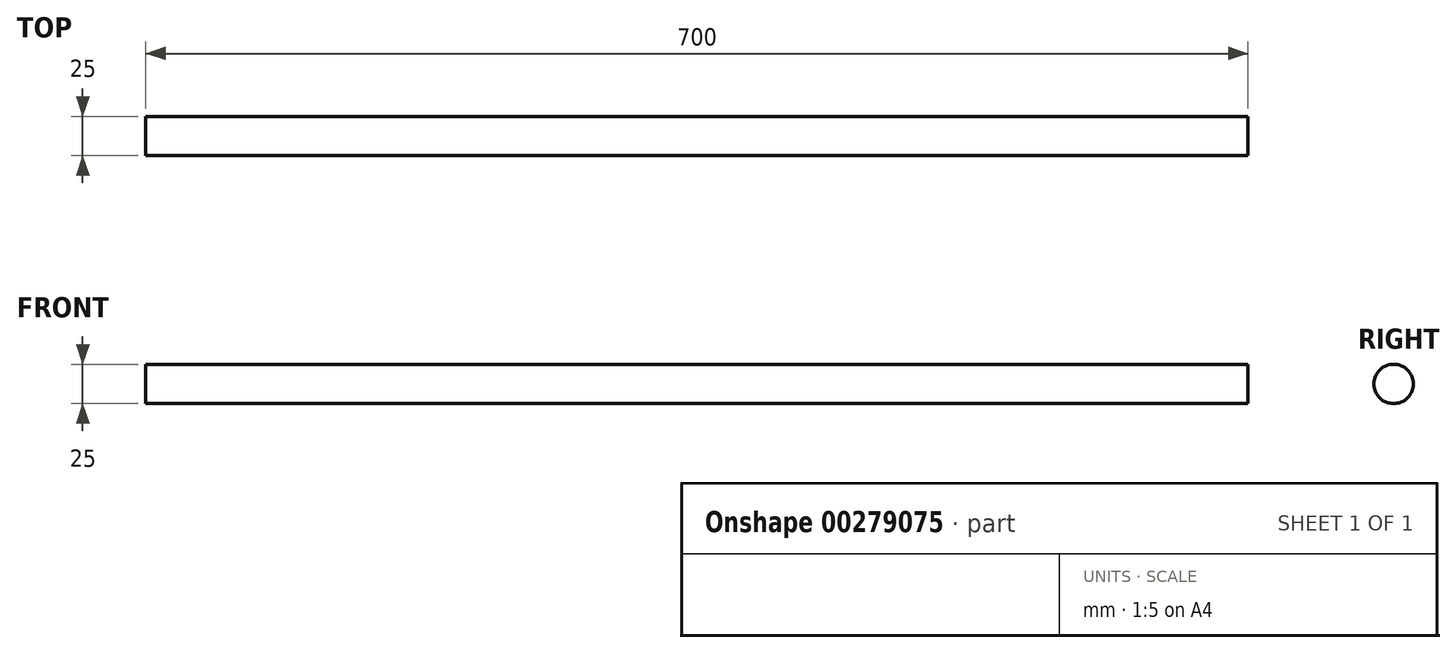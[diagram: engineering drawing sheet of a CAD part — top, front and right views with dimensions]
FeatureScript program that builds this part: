
annotation { "Feature Type Name" : "Feature", "Feature Type Description" : "" }
export const myFeature = defineFeature(function(context is Context, id is Id, definition is map)
    precondition{}
    {
        {
            var Q0;
            Q0=qCreatedBy(makeId("Right.planeOp"),FACE);
            var sketch = newSketch(context, id + "F0", { "sketchPlane" : qUnion([Q0])});
            skCircle(sketch, "E0", {"center": v(0, 0) * mm, "radius": 12.5 * mm});
            skSolve(sketch);
        }
        {
            var Q0;
            Q0=makeQuery(id+"F0.imprint","IMPRINT",FACE,{"disambiguationData":[TD([[makeQuery(id+"F0.imprint","IMPRINT",EDGE,{"derivedFrom":sQuery(id+"F0.wireOp",EDGE,"E0")}),1.0]])]});
            var Q1;
            Q1=sQuery(id+"F0.wireOp",EDGE,"E0");
            extrude(context, id + "F1", {"entities" : qUnion([Q0]), "surfaceEntities" : qUnion([Q1]), "depth" : .7 * 500 * mm, "hasSecondDirection" : true, "secondDirectionOppositeDirection" : true, "secondDirectionDepth" : 350 * mm});
        }
    });
